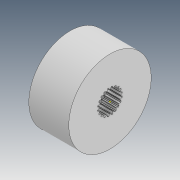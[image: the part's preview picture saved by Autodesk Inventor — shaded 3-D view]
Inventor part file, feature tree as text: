
AUTODESK INVENTOR PART (.ipt)
format: ipt  version: 2021 (Build 250183000, 183)  size: 295,424 bytes
history: native  units: in
note: dims shown in document units (in); Inventor stores cm internally (conversion verified against a paired STEP export)
features: sketch x4, extrude x3, other x2
ambient origin geometry x8: Origin, YZ Plane, XZ Plane, XY Plane, X Axis, Y Axis, Z Axis, Center Point
bodies: Body1 (feature_tree)
feature tree (9):
  other  "Sólido1"
  other  "Revolução1"
  extrude  "Extrusão1"  Depth=0.3858in
  extrude  "Extrusão2"  Depth=0.1378in
  extrude  "Extrusão5"  Depth=0.1909in
  sketch  "Esboço12"  dims[d7=0.0787in d8=0.0in d58=0.2008in d59=0.2323in d60=0.0024in d61=0.0024in d62=0.002in d63=0.002in d64=7.874in d66=360.0deg d68=0.1378in d69=0.0in d71=0.3346in d72=0.3543in d73=0.0344in d74=0.0344in]
  sketch  "Esboço2"  dims[d0=0.374in d1=0.3858in]
  sketch  "Esboço3"  dims[d2=90.0deg d3=0.1378in]
  sketch  "Esboço4"  dims[d4=0.1909in d5=0.0in d6=0.3543in]
